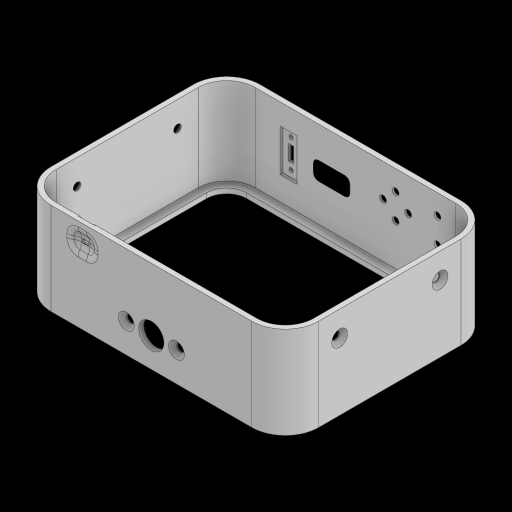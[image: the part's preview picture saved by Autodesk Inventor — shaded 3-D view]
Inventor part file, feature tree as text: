
AUTODESK INVENTOR PART (.ipt)
format: ipt  version: 2024 (Build 280153000, 153)  size: 474,624 bytes
history: native  units: mm
features: sketch x14, extrude x11, fillet x7, projected_geometry x4, chamfer x3, hole x3, shell x1
ambient origin geometry x8: Origin, YZ Plane, XZ Plane, XY Plane, X Axis, Y Axis, Z Axis, Center Point
bodies: Volumenkörper1 (feature_tree)
feature tree (43):
  extrude  "Extrusion1"  Depth=125.0mm
  shell  "Wandung1"  Thickness=55.0mm
  fillet  "Rundung1"  Radius=3.0mm
  fillet  "Rundung2"  Radius=17.0mm
  extrude  "Extrusion2"  Depth=5.0mm
  extrude  "Extrusion3"  Depth=3.0mm
  extrude  "Extrusion4"  Depth=4.0mm
  chamfer  "Fasen1"  Distance=3.0mm
  fillet  "Rundung3"  Radius=4.0mm
  chamfer  "Fasen2"  Distance=4.0mm
  fillet  "Rundung4"  Radius=25.0mm
  hole  "Bohrung1"  [1 undecoded]
  hole  "Bohrung2"  [1 undecoded]
  extrude  "Extrusion5"  Depth=2.0mm
  extrude  "Extrusion6"  Depth=2.0mm
  fillet  "Rundung5"  Radius=11.0mm
  chamfer  "Fasen3"  Distance=3.0mm
  fillet  "Rundung6"  Radius=3.0mm
  extrude  "Extrusion7"  Depth=5.0mm
  extrude  "Extrusion8"  Depth=3.0mm TaperAngle=45.0deg
  fillet  "Rundung7"  Radius=5.0mm
  extrude  "Extrusion10"  Depth=2.0mm
  hole  "Bohrung3"  [1 undecoded]
  extrude  "Extrusion11"  Depth=2.0mm
  extrude  "Extrusion12"  Depth=2.0mm
  sketch  "Skizze1"  dims[d0=160.0mm d1=125.0mm d2=55.0mm d3=0.0mm d4=3.0mm d5=17.0mm]
  sketch  "Skizze2"  dims[d6=20.0mm d7=5.0mm]
  sketch  "Skizze3"  dims[d8=3.0mm d9=0.0mm d10=56.0mm]
  sketch  "Skizze4"  dims[d11=12.0mm d12=4.0mm]
  sketch  "Skizze5"  dims[d13=4.0mm]
  sketch  "Skizze6"  dims[d14=15.0mm]
  sketch  "Skizze7"  dims[d15=56.0mm]
  sketch  "Skizze8"  dims[d16=4.0mm]
  sketch  "Skizze9"  dims[d17=7.5mm]
  sketch  "Skizze10"  dims[d18=7.5mm]
  projected_geometry  "Projizierte Kontur1"
  projected_geometry  "Projizierte Kontur2"
  projected_geometry  "Projizierte Kontur3"
  sketch  "Skizze12"  dims[d19=4.0mm]
  sketch  "Skizze13"  dims[d20=7.5mm]
  sketch  "Skizze14"  dims[d21=7.5mm d22=3.0mm d23=0.0mm d24=4.0mm]
  sketch  "Skizze15"  dims[d25=25.0mm d26=4.0mm d27=25.0mm d28=27.0mm d29=12.0mm d30=19.801mm d31=22.0mm d32=11.0mm d34=3.0mm d35=0.0mm d36=3.0mm d37=2.0mm d38=45.0deg d39=5.0mm d40=3.0mm d41=2.0mm d42=45.0deg d43=5.0mm d44=0.808mm d45=15.0mm d46=15.0mm d47=30.0mm d48=30.0mm d49=4.5mm d50=6.0mm d51=9.4mm d52=2.0mm d53=90.0deg d54=8.0mm d55=20.594885mm d56=30.0mm d57=30.0mm d58=15.0mm d59=15.0mm d60=4.5mm d61=6.0mm d62=9.4mm d63=2.0mm d64=90.0deg d65=8.0mm d66=20.594885mm d67=2.0mm d68=10.85mm d69=35.75mm d70=3.0mm d71=0.0mm d72=9.0mm d73=6.0mm d74=2.0mm d75=0.0mm d76=2.0mm d77=3.0mm d78=2.0mm d79=45.0deg d80=6.0mm d81=1.0mm d82=2.0mm d83=2.0mm d84=0.0mm d85=4.0mm d86=0.5mm d87=11.0mm d88=0.0mm d89=3.0mm d94=15.0mm d95=17.5mm d96=3.0mm d97=0.0mm d98=15.0mm d99=15.0mm d100=4.5mm d101=6.0mm d102=9.4mm d103=2.0mm d104=90.0deg d105=8.0mm d106=20.594885mm d107=10.0mm d108=25.0mm d109=30.0mm d110=20.0mm d111=1.5mm d112=0.0mm d113=3.0mm d114=9.0mm d115=2.5mm d116=2.5mm d117=8.5mm d118=8.5mm d119=2.0mm d120=0.0mm]
  projected_geometry  "Projizierte Kontur4"
note: 3 required parameter values undecoded (feature->parameter linkage not recoverable at this tier; creation-order binding heuristic only, values carry confidence <= 0.55)
